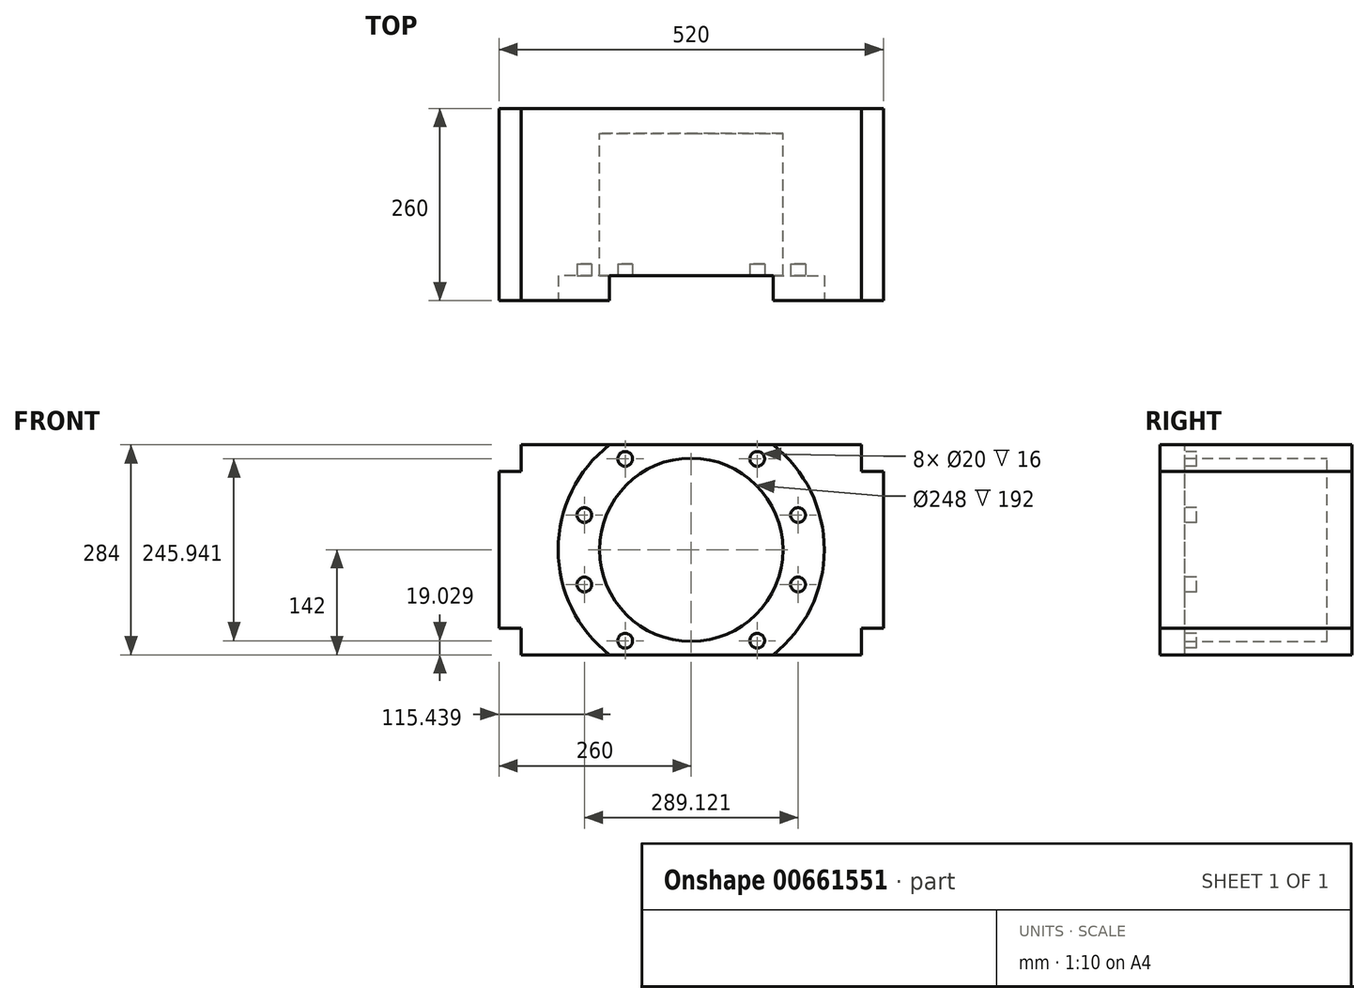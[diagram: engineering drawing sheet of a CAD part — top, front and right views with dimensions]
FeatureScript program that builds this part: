
annotation { "Feature Type Name" : "Feature", "Feature Type Description" : "" }
export const myFeature = defineFeature(function(context is Context, id is Id, definition is map)
    precondition{}
    {
        {
            var Q0;
            Q0=qCreatedBy(makeId("Front.planeOp"),FACE);
            var sketch = newSketch(context, id + "F0", { "sketchPlane" : qUnion([Q0])});
            skLineSegment(sketch, "E0.bottom", {"start": v(30, 0) * mm, "end": v(490, 0) * mm});
            skLineSegment(sketch, "E0.top", {"start": v(30, -284) * mm, "end": v(490, -284) * mm});
            skLineSegment(sketch, "E0.left", {"start": v(0, -36) * mm, "end": v(0, -248) * mm});
            skLineSegment(sketch, "E0.right", {"start": v(520, -36) * mm, "end": v(520, -248) * mm});
            skLineSegment(sketch, "E1", {"start": v(30, 0) * mm, "end": v(30, -36) * mm});
            skLineSegment(sketch, "E2", {"start": v(30, -36) * mm, "end": v(0, -36) * mm});
            skLineSegment(sketch, "E3", {"start": v(30, -284) * mm, "end": v(30, -248) * mm});
            skLineSegment(sketch, "E4", {"start": v(30, -248) * mm, "end": v(0, -248) * mm});
            skLineSegment(sketch, "E5", {"start": v(520, -248) * mm, "end": v(490, -248) * mm});
            skPoint(sketch, "E6.start.orphan", {"position": v(505, -266) * mm});
            skLineSegment(sketch, "E7", {"start": v(490, -248) * mm, "end": v(490, -284) * mm});
            skPoint(sketch, "E8.orphan", {"position": v(520, -284) * mm});
            skLineSegment(sketch, "E9", {"start": v(490, 0) * mm, "end": v(490, -36) * mm});
            skLineSegment(sketch, "E10", {"start": v(490, -36) * mm, "end": v(520, -36) * mm});
            skCircle(sketch, "E11", {"center": v(260, -142) * mm, "radius": 124 * mm});
            skPoint(sketch, "E11.centerSnap0", {"position": v(260, 0) * mm});
            skPoint(sketch, "E11.centerSnap1", {"position": v(0, -142) * mm});
            skSolve(sketch);
        }
        {
            var Q0;
            Q0=makeQuery(id+"F0.imprint","IMPRINT",FACE,{"disambiguationData":[TD([[makeQuery(id+"F0.imprint","IMPRINT",EDGE,{"derivedFrom":sQuery(id+"F0.wireOp",EDGE,"E0.bottom")}),-1.0]])]});
            extrude(context, id + "F1", {"entities" : qUnion([Q0]), "depth" : 260 * mm, "offsetDistance" : 25 * mm});
        }
        {
            var Q0;
            Q0=makeQuery(id+"F1.opExtrude","CAP_FACE",FACE,{"disambiguationData":[OSD([sQuery(id+"F0.wireOp",EDGE,"E0.bottom"),sQuery(id+"F0.wireOp",EDGE,"E0.top"),sQuery(id+"F0.wireOp",EDGE,"E0.left"),sQuery(id+"F0.wireOp",EDGE,"E0.right"),sQuery(id+"F0.wireOp",EDGE,"E1"),sQuery(id+"F0.wireOp",EDGE,"E2"),sQuery(id+"F0.wireOp",EDGE,"E3"),sQuery(id+"F0.wireOp",EDGE,"E4"),sQuery(id+"F0.wireOp",EDGE,"E5"),sQuery(id+"F0.wireOp",EDGE,"E7"),sQuery(id+"F0.wireOp",EDGE,"E9"),sQuery(id+"F0.wireOp",EDGE,"E10"),sQuery(id+"F0.wireOp",EDGE,"E11")])],"isStart":false});
            var sketch = newSketch(context, id + "F2", { "sketchPlane" : qUnion([Q0])});
            skArc(sketch, "E12", {"start": v(370.62, -284) * mm, "mid": v(440, -142) * mm, "end": v(370.62, 0) * mm});
            skLineSegment(sketch, "E13", {"start": v(149.38, 0) * mm, "end": v(370.62, 0) * mm});
            skLineSegment(sketch, "E14", {"start": v(370.62, 0) * mm, "end": v(370.62, 0) * mm});
            skLineSegment(sketch, "E15", {"start": v(149.38, -284) * mm, "end": v(370.62, -284) * mm});
            skArc(sketch, "E16.trimOffspring", {"start": v(149.38, 0) * mm, "mid": v(80, -142) * mm, "end": v(149.38, -284) * mm});
            skSolve(sketch);
        }
        {
            var Q0;
            Q0=makeQuery(id+"F2.imprint","IMPRINT",FACE,{"disambiguationData":[TD([[makeQuery(id+"F2.imprint","IMPRINT",EDGE,{"derivedFrom":sQuery(id+"F2.wireOp",EDGE,"E12")}),1.0]])]});
            extrude(context, id + "F3", {"entities" : qUnion([Q0]), "operationType" : NewBodyOperationType.REMOVE, "oppositeDirection" : true, "depth" : 34 * mm, "offsetDistance" : 25 * mm});
        }
        {
            var Q0;
            Q0=makeQuery(id+"F1.opExtrude","CAP_FACE",FACE,{"disambiguationData":[OSD([sQuery(id+"F0.wireOp",EDGE,"E0.bottom"),sQuery(id+"F0.wireOp",EDGE,"E0.top"),sQuery(id+"F0.wireOp",EDGE,"E0.left"),sQuery(id+"F0.wireOp",EDGE,"E0.right"),sQuery(id+"F0.wireOp",EDGE,"E1"),sQuery(id+"F0.wireOp",EDGE,"E2"),sQuery(id+"F0.wireOp",EDGE,"E3"),sQuery(id+"F0.wireOp",EDGE,"E4"),sQuery(id+"F0.wireOp",EDGE,"E5"),sQuery(id+"F0.wireOp",EDGE,"E7"),sQuery(id+"F0.wireOp",EDGE,"E9"),sQuery(id+"F0.wireOp",EDGE,"E10"),sQuery(id+"F0.wireOp",EDGE,"E11")])],"isStart":true});
            var sketch = newSketch(context, id + "F4", { "sketchPlane" : qUnion([Q0])});
            skCircle(sketch, "E17", {"center": v(-260, -142) * mm, "radius": 124 * mm});
            skSolve(sketch);
        }
        {
            var Q0;
            Q0=makeQuery(id+"F4.imprint","IMPRINT",FACE,{"disambiguationData":[TD([[makeQuery(id+"F4.imprint","IMPRINT",EDGE,{"derivedFrom":sQuery(id+"F4.wireOp",EDGE,"E17")}),-1.0]])]});
            extrude(context, id + "F5", {"entities" : qUnion([Q0]), "operationType" : NewBodyOperationType.ADD, "oppositeDirection" : true, "depth" : 34 * mm, "offsetDistance" : 25 * mm});
        }
        {
            var Q0;
            Q0=makeQuery(id+"F3.boolean.opBoolean","COPY",FACE,{"derivedFrom":makeQuery(id+"F3.opExtrude","CAP_FACE",FACE,{"disambiguationData":[OSD([sQuery(id+"F0.wireOp",EDGE,"E11"),sQuery(id+"F2.wireOp",EDGE,"E12"),sQuery(id+"F2.wireOp",EDGE,"E13"),sQuery(id+"F2.wireOp",EDGE,"E15"),sQuery(id+"F2.wireOp",EDGE,"E16.trimOffspring")])],"isStart":false})});
            var sketch = newSketch(context, id + "F6", { "sketchPlane" : qUnion([Q0])});
            skPoint(sketch, "E18.center.orphan", {"position": v(260, -142) * mm});
            skPoint(sketch, "E19.center.orphan", {"position": v(420, -142) * mm});
            skPoint(sketch, "E20.centerSnap0", {"position": v(260, -284) * mm});
            skPoint(sketch, "E20.center.orphan", {"position": v(260, -302) * mm});
            skPoint(sketch, "E21.centerSnap0", {"position": v(260, 0) * mm});
            skCircle(sketch, "E22.1.0", {"center": v(170.66, -19.03) * mm, "radius": 10 * mm});
            skCircle(sketch, "E22.2.0", {"center": v(115.44, -95.03) * mm, "radius": 10 * mm});
            skCircle(sketch, "E22.3.0", {"center": v(115.44, -188.97) * mm, "radius": 10 * mm});
            skCircle(sketch, "E22.4.0", {"center": v(170.66, -264.97) * mm, "radius": 10 * mm});
            skCircle(sketch, "E22.6.0", {"center": v(349.34, -264.97) * mm, "radius": 10 * mm});
            skCircle(sketch, "E22.7.0", {"center": v(404.56, -188.97) * mm, "radius": 10 * mm});
            skCircle(sketch, "E22.8.0", {"center": v(404.56, -95.03) * mm, "radius": 10 * mm});
            skCircle(sketch, "E22.9.0", {"center": v(349.34, -19.03) * mm, "radius": 10 * mm});
            skPoint(sketch, "E21.center.orphan", {"position": v(260, 10) * mm});
            skSolve(sketch);
        }
        {
            var Q0;
            Q0 = qSketchRegion(id + "F6", true);
            extrude(context, id + "F7", {"entities" : qUnion([Q0]), "operationType" : NewBodyOperationType.REMOVE, "oppositeDirection" : true, "depth" : 16 * mm, "offsetDistance" : 25 * mm});
        }
    });
